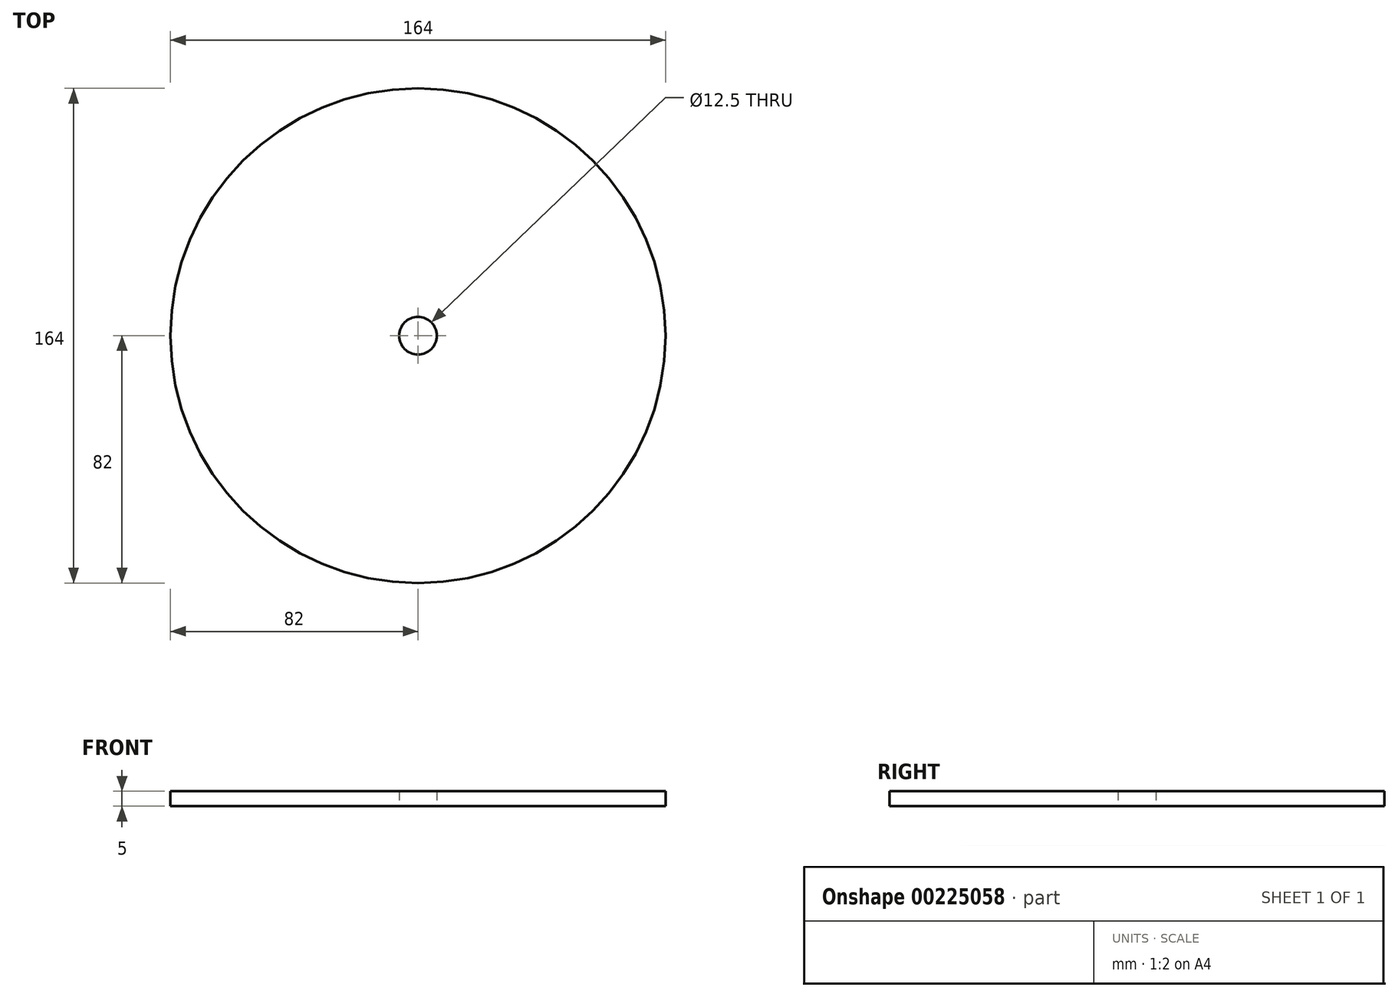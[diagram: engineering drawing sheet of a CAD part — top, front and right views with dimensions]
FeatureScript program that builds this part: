
annotation { "Feature Type Name" : "Feature", "Feature Type Description" : "" }
export const myFeature = defineFeature(function(context is Context, id is Id, definition is map)
    precondition{}
    {
        {
            var Q0;
            Q0=qCreatedBy(makeId("Top.planeOp"),FACE);
            var sketch = newSketch(context, id + "F0", { "sketchPlane" : qUnion([Q0])});
            skCircle(sketch, "E0", {"center": v(0, 0) * mm, "radius": 82 * mm});
            skCircle(sketch, "E1", {"center": v(0, 0) * mm, "radius": 6.25 * mm});
            skSolve(sketch);
        }
        {
            var Q0;
            Q0=qSketchRegion(id+"F0",true);
            extrude(context, id + "F1", {"entities" : qUnion([Q0]), "depth" : 5 * mm});
        }
    });
